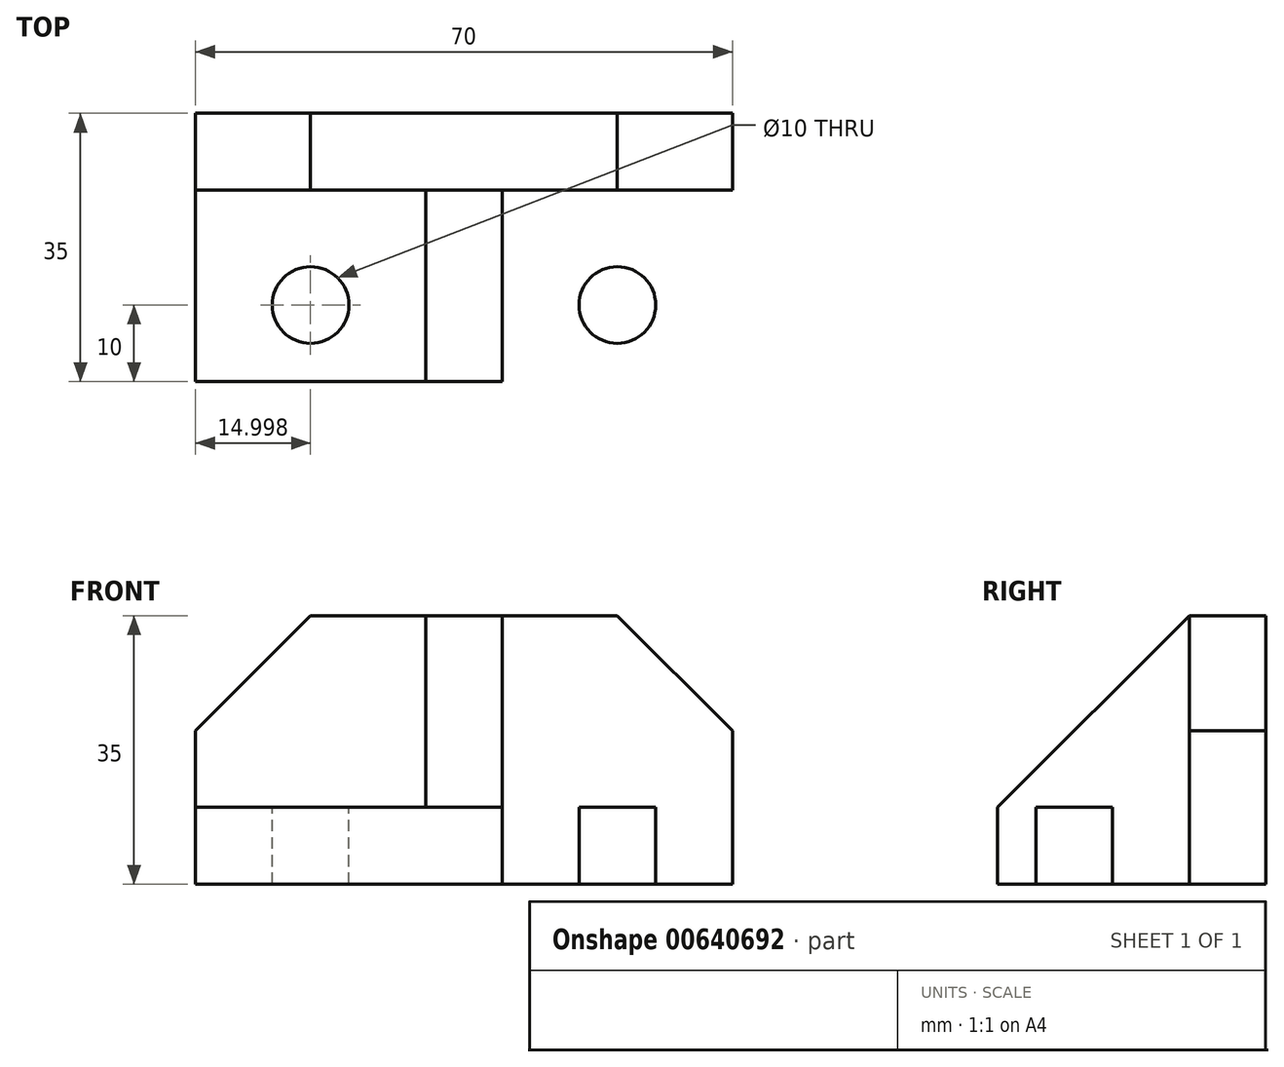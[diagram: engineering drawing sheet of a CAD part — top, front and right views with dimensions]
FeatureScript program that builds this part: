
annotation { "Feature Type Name" : "Feature", "Feature Type Description" : "" }
export const myFeature = defineFeature(function(context is Context, id is Id, definition is map)
    precondition{}
    {
        {
            var Q0;
            Q0=qCreatedBy(makeId("Front.planeOp"),FACE);
            var sketch = newSketch(context, id + "F0", { "sketchPlane" : qUnion([Q0])});
            skLineSegment(sketch, "E0.bottom", {"start": v(-26.5, -1.5) * mm, "end": v(43.5, -1.5) * mm});
            skLineSegment(sketch, "E0.top", {"start": v(-26.5, -11.5) * mm, "end": v(43.5, -11.5) * mm});
            skLineSegment(sketch, "E0.left", {"start": v(-26.5, -1.5) * mm, "end": v(-26.5, -11.5) * mm});
            skLineSegment(sketch, "E0.right", {"start": v(43.5, -1.5) * mm, "end": v(43.5, -11.5) * mm});
            skSolve(sketch);
        }
        {
            var Q0;
            Q0 = qSketchRegion(id + "F0", true);
            extrude(context, id + "F1", {"entities" : qUnion([Q0]), "oppositeDirection" : true, "depth" : 35 * mm, "offsetDistance" : 25 * mm});
        }
        {
            var Q0;
            Q0=makeQuery(id+"F1.opExtrude","SWEPT_FACE",FACE,{"disambiguationData":[OSD([sQuery(id+"F0.wireOp",EDGE,"E0.bottom")])]});
            var sketch = newSketch(context, id + "F2", { "sketchPlane" : qUnion([Q0])});
            skLineSegment(sketch, "E1.bottom", {"start": v(-26.5, 35) * mm, "end": v(43.5, 35) * mm});
            skLineSegment(sketch, "E1.top", {"start": v(-26.5, 25) * mm, "end": v(43.5, 25) * mm});
            skLineSegment(sketch, "E1.left", {"start": v(-26.5, 35) * mm, "end": v(-26.5, 25) * mm});
            skLineSegment(sketch, "E1.right", {"start": v(43.5, 35) * mm, "end": v(43.5, 25) * mm});
            skLineSegment(sketch, "E2", {"start": v(-11.5, 25) * mm, "end": v(-11.5, 10) * mm, "construction": true});
            skCircle(sketch, "E3", {"center": v(-11.5, 10) * mm, "radius": 5 * mm});
            skLineSegment(sketch, "E4", {"start": v(8.5, 0) * mm, "end": v(8.5, 25) * mm, "construction": true});
            skLineSegment(sketch, "E5.0", {"start": v(13.5, 0) * mm, "end": v(13.5, 25) * mm});
            skLineSegment(sketch, "E6.0", {"start": v(3.5, 0) * mm, "end": v(3.5, 25) * mm});
            skCircle(sketch, "E7.MirrorC", {"center": v(28.5, 10) * mm, "radius": 5 * mm});
            skSolve(sketch);
        }
        {
            var Q0;
            Q0=makeQuery(id+"F2.imprint","IMPRINT",FACE,{"disambiguationData":[TD([[makeQuery(id+"F2.imprint","IMPRINT",EDGE,{"derivedFrom":sQuery(id+"F2.wireOp",EDGE,"E1.bottom")}),-1.0]])]});
            extrude(context, id + "F3", {"entities" : qUnion([Q0]), "operationType" : NewBodyOperationType.ADD, "depth" : 25 * mm, "offsetDistance" : 25 * mm});
        }
        {
            var Q0;
            {var subQ0=sQuery(id+"F2.wireOp",EDGE,"E5.0");Q0=makeQuery(id+"F2.imprint","IMPRINT",FACE,{"disambiguationData":[TD([[makeQuery(id+"F2.imprint","IMPRINT",EDGE,{"derivedFrom":subQ0}),1.0]])]});}
            extrude(context, id + "F4", {"entities" : qUnion([Q0]), "operationType" : NewBodyOperationType.ADD, "depth" : 25 * mm, "offsetDistance" : 25 * mm});
        }
        {
            var Q0;
            Q0=makeQuery(id+"F4.opExtrude","SWEPT_FACE",FACE,{"disambiguationData":[OSD([sQuery(id+"F2.wireOp",EDGE,"E6.0")])]});
            var sketch = newSketch(context, id + "F5", { "sketchPlane" : qUnion([Q0])});
            skLineSegment(sketch, "E8", {"start": v(-25, 23.5) * mm, "end": v(0, -1.5) * mm});
            skSolve(sketch);
        }
        {
            var Q0;
            Q0=makeQuery(id+"F5.imprint","IMPRINT",FACE,{"disambiguationData":[TD([[makeQuery(id+"F5.imprint","IMPRINT",EDGE,{"derivedFrom":sQuery(id+"F5.wireOp",EDGE,"E8")}),1.0]])]});
            extrude(context, id + "F6", {"entities" : qUnion([Q0]), "operationType" : NewBodyOperationType.REMOVE, "endBound" : BoundingType.UP_TO_NEXT, "oppositeDirection" : true, "depth" : 25 * mm, "offsetDistance" : 25 * mm});
        }
        {
            var Q0;
            Q0=makeQuery(id+"F2.imprint","IMPRINT",FACE,{"disambiguationData":[TD([[makeQuery(id+"F2.imprint","IMPRINT",EDGE,{"derivedFrom":sQuery(id+"F2.wireOp",EDGE,"E7.MirrorC")}),-1.0]])]});
            var Q1;
            Q1=makeQuery(id+"F2.imprint","IMPRINT",FACE,{"disambiguationData":[TD([[makeQuery(id+"F2.imprint","IMPRINT",EDGE,{"derivedFrom":sQuery(id+"F2.wireOp",EDGE,"E3")}),1.0]])]});
            extrude(context, id + "F7", {"entities" : qUnion([Q0, Q1]), "operationType" : NewBodyOperationType.REMOVE, "oppositeDirection" : true, "depth" : 25 * mm, "offsetDistance" : 25 * mm});
        }
        {
            var Q0;
            {var subQ1=sQuery(id+"F2.wireOp",EDGE,"E1.top");Q0=makeQuery(id+"F4.boolean.opBoolean","SPLIT",FACE,{"disambiguationData":[TD([makeQuery(id+"F1.opExtrude","SWEPT_FACE",FACE,{"disambiguationData":[OSD([sQuery(id+"F0.wireOp",EDGE,"E0.right")])]})])],"derivedFrom":makeQuery(id+"F3.opExtrude","SWEPT_FACE",FACE,{"disambiguationData":[OSD([subQ1])]})});}
            var sketch = newSketch(context, id + "F8", { "sketchPlane" : qUnion([Q0])});
            skLineSegment(sketch, "E9", {"start": v(43.5, 23.5) * mm, "end": v(28.5, 23.5) * mm});
            skLineSegment(sketch, "E10", {"start": v(43.5, 23.5) * mm, "end": v(43.5, 8.5) * mm});
            skLineSegment(sketch, "E11", {"start": v(28.5, 23.5) * mm, "end": v(43.5, 8.5) * mm});
            skLineSegment(sketch, "E12", {"start": v(8.5, 23.5) * mm, "end": v(8.5, -1.5) * mm, "construction": true});
            skLineSegment(sketch, "E13.MirrorCS", {"start": v(-26.5, 23.5) * mm, "end": v(-11.5, 23.5) * mm});
            skLineSegment(sketch, "E14.MirrorCS", {"start": v(-11.5, 23.5) * mm, "end": v(-26.5, 8.5) * mm});
            skLineSegment(sketch, "E15.MirrorCS", {"start": v(-26.5, 23.5) * mm, "end": v(-26.5, 8.5) * mm});
            skSolve(sketch);
        }
        {
            var Q0;
            Q0 = qSketchRegion(id + "F8", true);
            extrude(context, id + "F9", {"entities" : qUnion([Q0]), "operationType" : NewBodyOperationType.REMOVE, "oppositeDirection" : true, "depth" : 25 * mm, "offsetDistance" : 25 * mm});
        }
    });
